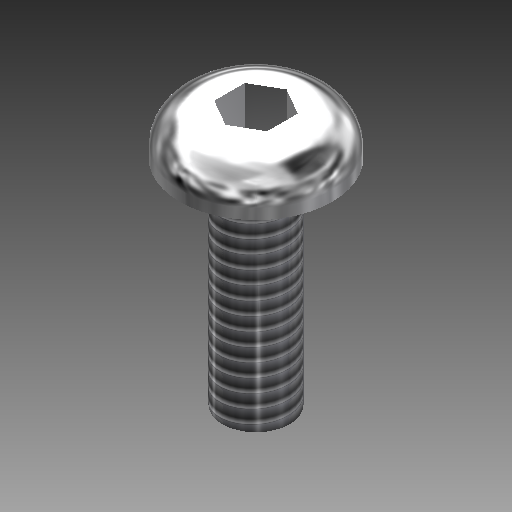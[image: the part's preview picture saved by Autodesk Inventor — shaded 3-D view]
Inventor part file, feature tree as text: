
AUTODESK INVENTOR PART (.ipt)
format: ipt  version: 2018 (Build 220112000, 112)  size: 179,712 bytes
history: native  units: in
note: dims shown in document units (in); Inventor stores cm internally (conversion verified against a paired STEP export)
features: extrude x2, sketch x2, fillet x1, thread x1
ambient origin geometry x8: Origin, YZ Plane, XZ Plane, XY Plane, X Axis, Y Axis, Z Axis, Center Point
bodies: Solid1 (feature_tree)
feature tree (6):
  extrude  "Extrusion1"  Depth=0.315in TaperAngle=0.0deg
  extrude  "Extrusion2"  Depth=0.05in
  fillet  "Fillet1"  Radius=0.05in
  thread  "Thread1"  [1 undecoded]
  sketch  "Sketch1"  dims[d0=0.099in d1=0.315in d2=0.0in]
  sketch  "Sketch2"  dims[d5=0.065in d6=0.0in d7=0.039in d8=0.05in d9=1.0in d10=0.0in]
note: 1 required parameter value undecoded (feature->parameter linkage not recoverable at this tier; creation-order binding heuristic only, values carry confidence <= 0.55)
